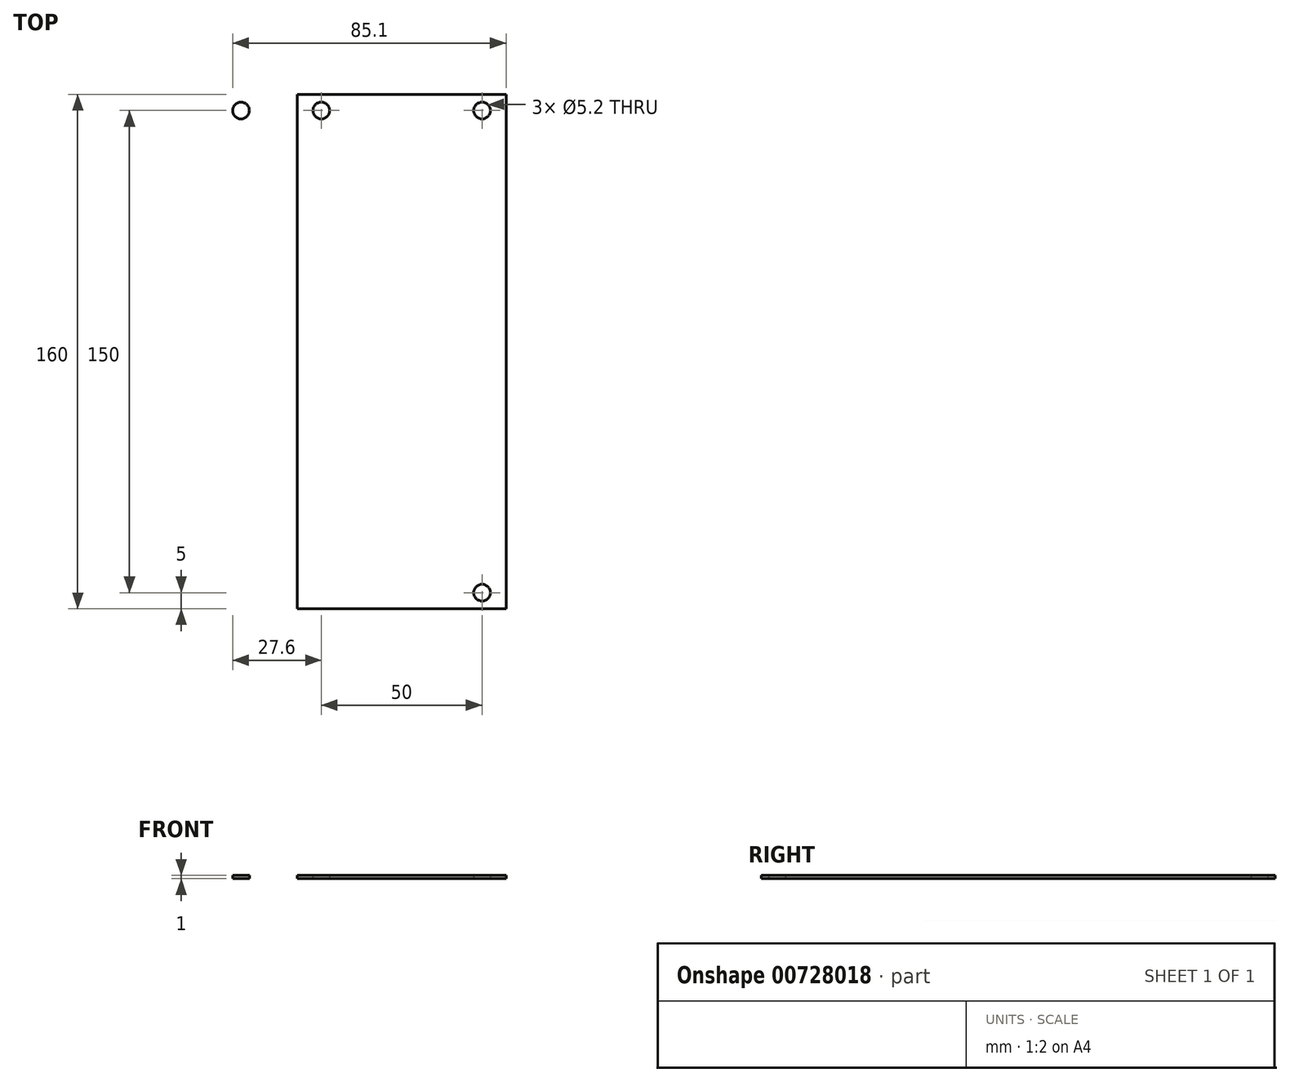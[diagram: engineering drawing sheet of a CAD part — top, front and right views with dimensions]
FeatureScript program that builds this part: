
annotation { "Feature Type Name" : "Feature", "Feature Type Description" : "" }
export const myFeature = defineFeature(function(context is Context, id is Id, definition is map)
    precondition{}
    {
        {
            var Q0;
            Q0=qCreatedBy(makeId("Top.planeOp"),FACE);
            var sketch = newSketch(context, id + "F0", { "sketchPlane" : qUnion([Q0])});
            skLineSegment(sketch, "E0.bottom", {"start": v(5, 0) * mm, "end": v(70, 0) * mm});
            skLineSegment(sketch, "E0.top", {"start": v(5, 160) * mm, "end": v(70, 160) * mm});
            skLineSegment(sketch, "E0.left", {"start": v(5, 0) * mm, "end": v(5, 160) * mm});
            skLineSegment(sketch, "E0.right", {"start": v(70, 0) * mm, "end": v(70, 160) * mm});
            skCircle(sketch, "E1", {"center": v(12.5, 155) * mm, "radius": 2.6 * mm});
            skCircle(sketch, "E2", {"center": v(62.5, 155) * mm, "radius": 2.6 * mm});
            skCircle(sketch, "E3", {"center": v(62.5, 5) * mm, "radius": 2.6 * mm});
            skLineSegment(sketch, "E4", {"start": v(0, 0) * mm, "end": v(0, 160) * mm});
            skCircle(sketch, "E5.MirrorC", {"center": v(-12.5, 155) * mm, "radius": 2.6 * mm});
            skCircle(sketch, "E6.MirrorC", {"center": v(-62.5, 155) * mm, "radius": 2.6 * mm});
            skLineSegment(sketch, "E7.MirrorCS", {"start": v(-5, 0) * mm, "end": v(-70, 0) * mm});
            skLineSegment(sketch, "E8.MirrorCS", {"start": v(-5, 160) * mm, "end": v(-70, 160) * mm});
            skLineSegment(sketch, "E9.MirrorCS", {"start": v(-70, 0) * mm, "end": v(-70, 160) * mm});
            skLineSegment(sketch, "E10.MirrorCS", {"start": v(-5, 0) * mm, "end": v(-5, 160) * mm});
            skCircle(sketch, "E11.MirrorC", {"center": v(-62.5, 5) * mm, "radius": 2.6 * mm});
            skSolve(sketch);
        }
        {
            var Q0;
            Q0=makeQuery(id+"F0.imprint","IMPRINT",FACE,{"disambiguationData":[TD([[makeQuery(id+"F0.imprint","IMPRINT",EDGE,{"derivedFrom":sQuery(id+"F0.wireOp",EDGE,"E0.bottom")}),1.0]])]});
            var Q1;
            Q1=makeQuery(id+"F0.imprint","IMPRINT",FACE,{"disambiguationData":[TD([[makeQuery(id+"F0.imprint","IMPRINT",EDGE,{"derivedFrom":sQuery(id+"F0.wireOp",EDGE,"E5.MirrorC")}),1.0]])]});
            extrude(context, id + "F1", {"entities" : qUnion([Q0, Q1]), "depth" : 1 * mm, "offsetDistance" : 25 * mm});
        }
    });
